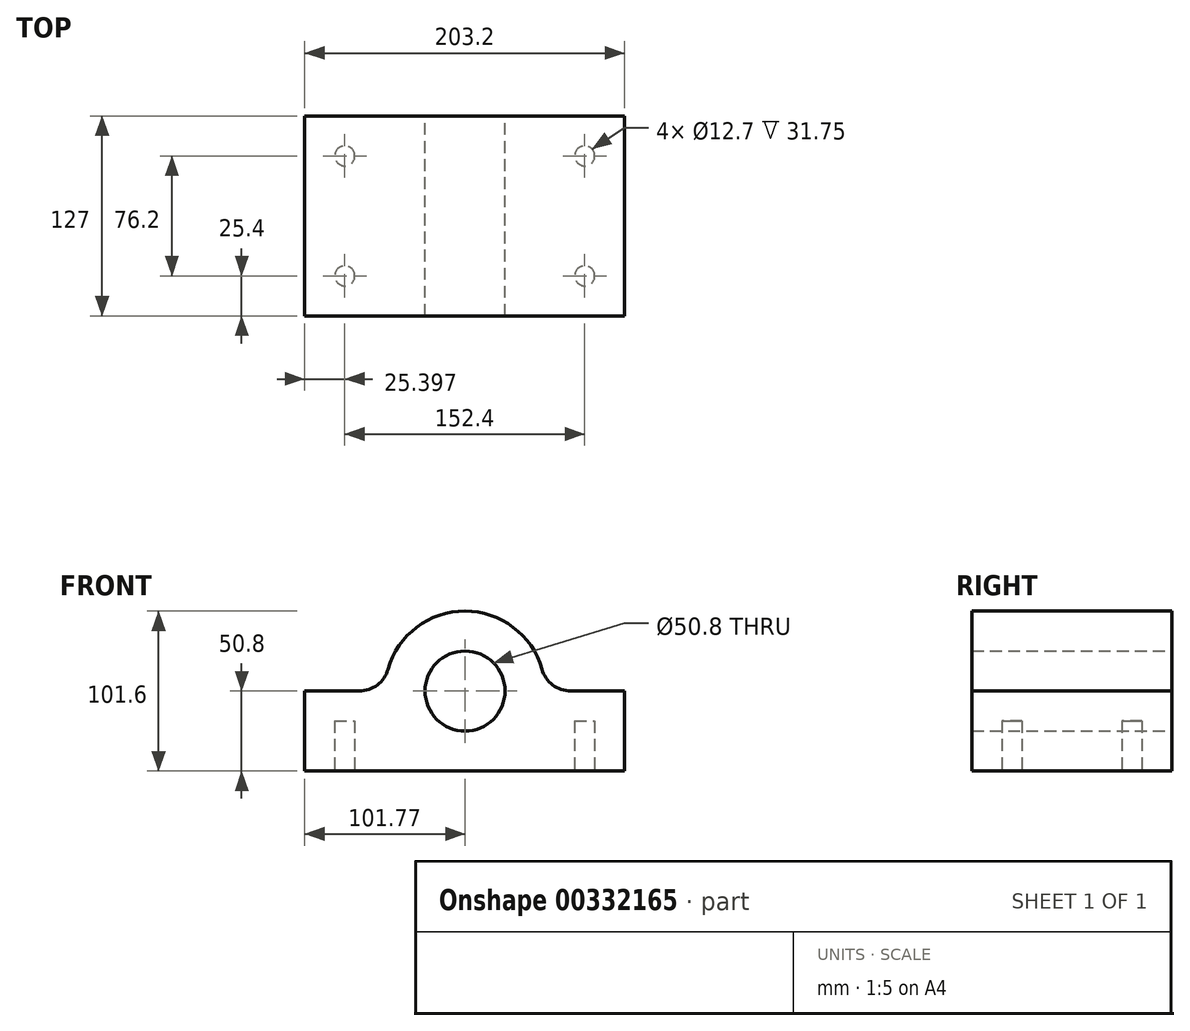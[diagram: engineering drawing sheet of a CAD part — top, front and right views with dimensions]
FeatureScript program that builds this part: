
annotation { "Feature Type Name" : "Feature", "Feature Type Description" : "" }
export const myFeature = defineFeature(function(context is Context, id is Id, definition is map)
    precondition{}
    {
        {
            var Q0;
            Q0=qCreatedBy(makeId("Front.planeOp"),FACE);
            var sketch = newSketch(context, id + "F0", { "sketchPlane" : qUnion([Q0])});
            skCircle(sketch, "E0", {"center": v(0, 0) * mm, "radius": 25.4 * mm});
            skLineSegment(sketch, "E1", {"start": v(101.43, 0) * mm, "end": v(101.43, -50.8) * mm});
            skLineSegment(sketch, "E2", {"start": v(101.43, -50.8) * mm, "end": v(-101.77, -50.8) * mm});
            skLineSegment(sketch, "E3", {"start": v(-101.77, -50.8) * mm, "end": v(-101.77, 0) * mm});
            skLineSegment(sketch, "E4", {"start": v(-101.77, 0) * mm, "end": v(-67.2, 0) * mm});
            skArc(sketch, "E5", {"start": v(48.87, 13.85) * mm, "mid": v(0, 50.8) * mm, "end": v(-48.87, 13.85) * mm});
            skArc(sketch, "E6", {"start": v(-67.2, 0) * mm, "mid": v(-55.71, 3.85) * mm, "end": v(-48.87, 13.85) * mm});
            skArc(sketch, "E7", {"start": v(48.87, 13.85) * mm, "mid": v(55.71, 3.85) * mm, "end": v(67.2, 0) * mm});
            skLineSegment(sketch, "E8.trimOffspring", {"start": v(67.2, 0) * mm, "end": v(101.43, 0) * mm});
            skSolve(sketch);
        }
        {
            var Q0;
            Q0=makeQuery(id+"F0.imprint","IMPRINT",FACE,{"disambiguationData":[TD([[makeQuery(id+"F0.imprint","IMPRINT",EDGE,{"derivedFrom":sQuery(id+"F0.wireOp",EDGE,"E0")}),-1.0]])]});
            extrude(context, id + "F1", {"entities" : qUnion([Q0]), "depth" : 127 * mm});
        }
        {
            var Q0;
            Q0=makeQuery(id+"F1.opExtrude","SWEPT_FACE",FACE,{"disambiguationData":[OSD([sQuery(id+"F0.wireOp",EDGE,"E2")])]});
            var sketch = newSketch(context, id + "F2", { "sketchPlane" : qUnion([Q0])});
            skCircle(sketch, "E9", {"center": v(76.03, 101.6) * mm, "radius": 6.35 * mm});
            skCircle(sketch, "E10", {"center": v(76.03, 25.4) * mm, "radius": 6.35 * mm});
            skCircle(sketch, "E11", {"center": v(-76.37, 101.6) * mm, "radius": 6.35 * mm});
            skCircle(sketch, "E12", {"center": v(-76.37, 25.4) * mm, "radius": 6.35 * mm});
            skSolve(sketch);
        }
        {
            var Q0;
            Q0=makeQuery(id+"F2.imprint","IMPRINT",FACE,{"disambiguationData":[TD([[makeQuery(id+"F2.imprint","IMPRINT",EDGE,{"derivedFrom":sQuery(id+"F2.wireOp",EDGE,"E11")}),1.0]])]});
            var Q1;
            Q1=makeQuery(id+"F2.imprint","IMPRINT",FACE,{"disambiguationData":[TD([[makeQuery(id+"F2.imprint","IMPRINT",EDGE,{"derivedFrom":sQuery(id+"F2.wireOp",EDGE,"E12")}),1.0]])]});
            var Q2;
            Q2=makeQuery(id+"F2.imprint","IMPRINT",FACE,{"disambiguationData":[TD([[makeQuery(id+"F2.imprint","IMPRINT",EDGE,{"derivedFrom":sQuery(id+"F2.wireOp",EDGE,"E9")}),1.0]])]});
            var Q3;
            Q3=makeQuery(id+"F2.imprint","IMPRINT",FACE,{"disambiguationData":[TD([[makeQuery(id+"F2.imprint","IMPRINT",EDGE,{"derivedFrom":sQuery(id+"F2.wireOp",EDGE,"E10")}),1.0]])]});
            extrude(context, id + "F3", {"entities" : qUnion([Q0, Q1, Q2, Q3]), "operationType" : NewBodyOperationType.REMOVE, "oppositeDirection" : true, "depth" : 31.75 * mm});
        }
    });
